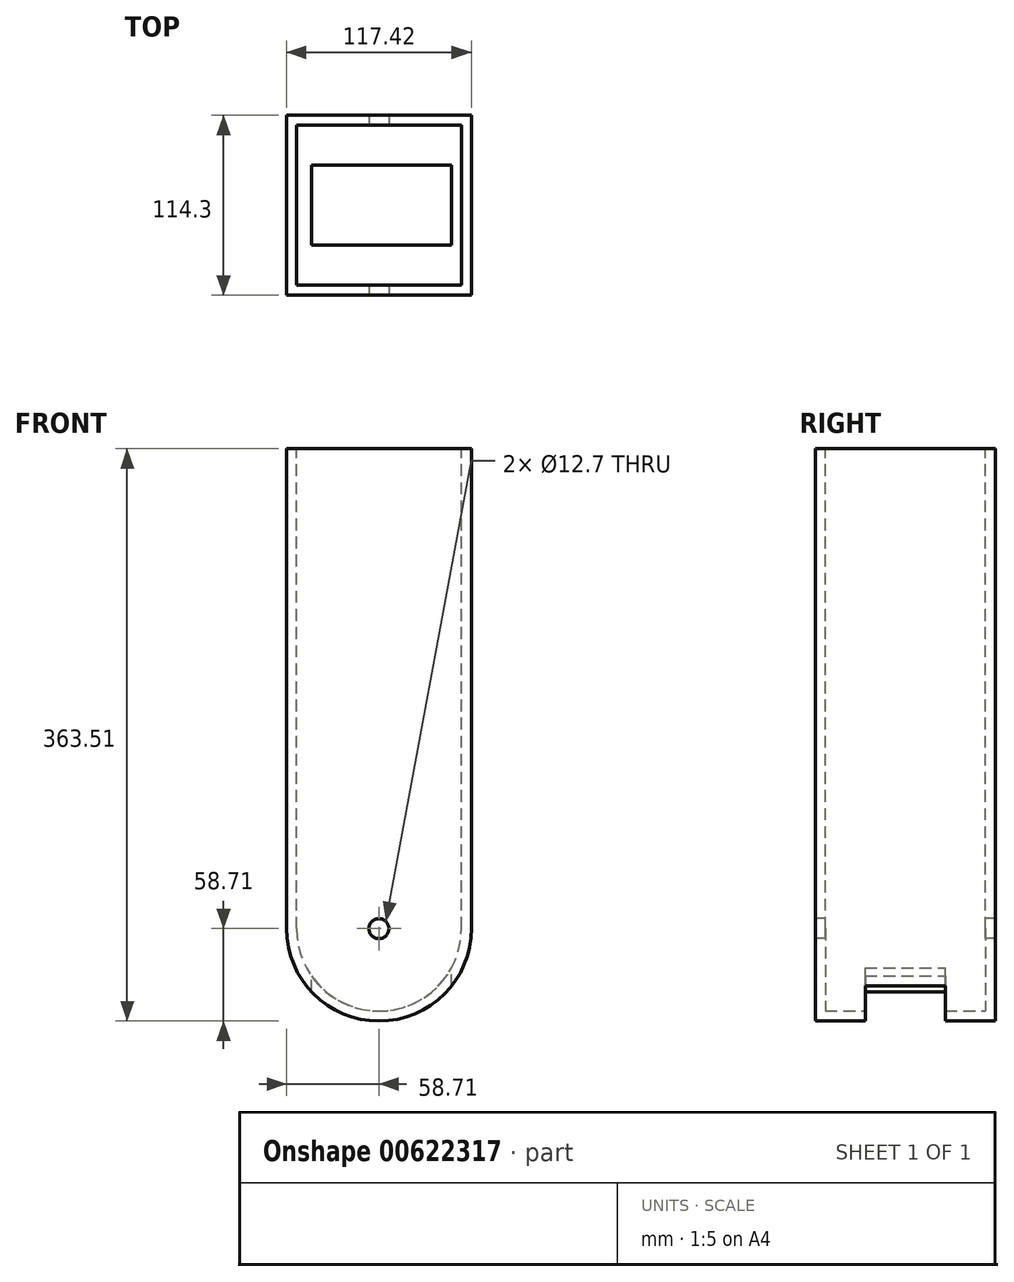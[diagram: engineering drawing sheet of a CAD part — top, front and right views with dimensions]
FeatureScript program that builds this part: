
annotation { "Feature Type Name" : "Feature", "Feature Type Description" : "" }
export const myFeature = defineFeature(function(context is Context, id is Id, definition is map)
    precondition{}
    {
        {
            var Q0;
            Q0=qCreatedBy(makeId("Front.planeOp"),FACE);
            var sketch = newSketch(context, id + "F0", { "sketchPlane" : qUnion([Q0])});
            skCircle(sketch, "E0", {"center": v(0, 0) * mm, "radius": 52.36 * mm});
            skLineSegment(sketch, "E1", {"start": v(-52.36, 0) * mm, "end": v(-52.36, 304.8) * mm});
            skLineSegment(sketch, "E2", {"start": v(52.36, 0) * mm, "end": v(52.36, 304.8) * mm});
            skLineSegment(sketch, "E3", {"start": v(-52.36, 304.8) * mm, "end": v(52.36, 304.8) * mm});
            skSolve(sketch);
        }
        {
            var Q0;
            {var subQ0=sQuery(id+"F0.wireOp",EDGE,"E0");var subQ1=makeQuery(id+"F0.imprint","INTERSECT",VERTEX,{"derivedFrom":[subQ0,sQuery(id+"F0.wireOp",EDGE,"E1")]});Q0=makeQuery(id+"F0.imprint","IMPRINT",FACE,{"disambiguationData":[TD([[makeQuery(id+"F0.imprint","IMPRINT",EDGE,{"disambiguationData":[TD([[subQ1,1.0]])],"derivedFrom":subQ0}),1.0]])]});}
            extrude(context, id + "F1", {"entities" : qUnion([Q0]), "depth" : 101.6 * mm, "offsetDistance" : 25.4 * mm, "symmetric" : true});
        }
        {
            var Q0;
            {var subQ0=sQuery(id+"F0.wireOp",EDGE,"E1");Q0=makeQuery(id+"F0.imprint","IMPRINT",FACE,{"disambiguationData":[TD([[makeQuery(id+"F0.imprint","IMPRINT",EDGE,{"derivedFrom":subQ0}),-1.0]])]});}
            extrude(context, id + "F2", {"entities" : qUnion([Q0]), "operationType" : NewBodyOperationType.ADD, "depth" : 50.8 * mm, "offsetDistance" : 25.4 * mm});
        }
        {
            var Q0;
            {var subQ0=sQuery(id+"F0.wireOp",EDGE,"E1");Q0=makeQuery(id+"F0.imprint","IMPRINT",FACE,{"disambiguationData":[TD([[makeQuery(id+"F0.imprint","IMPRINT",EDGE,{"derivedFrom":subQ0}),-1.0]])]});}
            extrude(context, id + "F3", {"entities" : qUnion([Q0]), "operationType" : NewBodyOperationType.ADD, "oppositeDirection" : true, "depth" : 50.8 * mm, "offsetDistance" : 25.4 * mm});
        }
        {
            var Q0;
            Q0=makeQuery(id+"F2.opExtrude","SWEPT_FACE",FACE,{"disambiguationData":[OSD([sQuery(id+"F0.wireOp",EDGE,"E3")])]});
            shell(context, id + "F4", {"entities" : qUnion([Q0]), "thickness" : 6.35 * mm, "oppositeDirection" : true});
        }
        {
            var Q0;
            {var subQ0=sQuery(id+"F0.wireOp",EDGE,"E0");Q0=makeQuery(id+"F2.boolean.opBoolean","MERGE",FACE,{"derivedFrom":[makeQuery(id+"F1.opExtrude","CAP_FACE",FACE,{"disambiguationData":[OSD([subQ0])],"isStart":false}),makeQuery(id+"F2.opExtrude","CAP_FACE",FACE,{"disambiguationData":[OSD([subQ0,sQuery(id+"F0.wireOp",EDGE,"E1"),sQuery(id+"F0.wireOp",EDGE,"E2"),sQuery(id+"F0.wireOp",EDGE,"E3")])],"isStart":false})]});}
            var sketch = newSketch(context, id + "F5", { "sketchPlane" : qUnion([Q0])});
            skCircle(sketch, "E4", {"center": v(0, 0) * mm, "radius": 6.35 * mm});
            skSolve(sketch);
        }
        {
            var Q0;
            Q0=makeQuery(id+"F5.imprint","IMPRINT",FACE,{"disambiguationData":[TD([[makeQuery(id+"F5.imprint","IMPRINT",EDGE,{"derivedFrom":sQuery(id+"F5.wireOp",EDGE,"E4")}),1.0]])]});
            extrude(context, id + "F6", {"entities" : qUnion([Q0]), "operationType" : NewBodyOperationType.REMOVE, "endBound" : BoundingType.THROUGH_ALL, "oppositeDirection" : true, "depth" : 25.4 * mm, "offsetDistance" : 25.4 * mm});
        }
        {
            var Q0;
            Q0=qCreatedBy(makeId("Top.planeOp"),FACE);
            var sketch = newSketch(context, id + "F7", { "sketchPlane" : qUnion([Q0])});
            skLineSegment(sketch, "E5.bottom", {"start": v(-42.89, 25.4) * mm, "end": v(46.01, 25.4) * mm});
            skLineSegment(sketch, "E5.top", {"start": v(-42.89, -25.4) * mm, "end": v(46.01, -25.4) * mm});
            skLineSegment(sketch, "E5.left", {"start": v(-42.89, 25.4) * mm, "end": v(-42.89, -25.4) * mm});
            skLineSegment(sketch, "E5.right", {"start": v(46.01, 25.4) * mm, "end": v(46.01, -25.4) * mm});
            skSolve(sketch);
        }
        {
            var Q0;
            Q0=makeQuery(id+"F7.imprint","IMPRINT",FACE,{"disambiguationData":[TD([[makeQuery(id+"F7.imprint","IMPRINT",EDGE,{"derivedFrom":sQuery(id+"F7.wireOp",EDGE,"E5.bottom")}),-1.0]])]});
            extrude(context, id + "F8", {"entities" : qUnion([Q0]), "operationType" : NewBodyOperationType.REMOVE, "endBound" : BoundingType.THROUGH_ALL, "oppositeDirection" : true, "depth" : 25.4 * mm, "offsetDistance" : 25.4 * mm});
        }
    });
